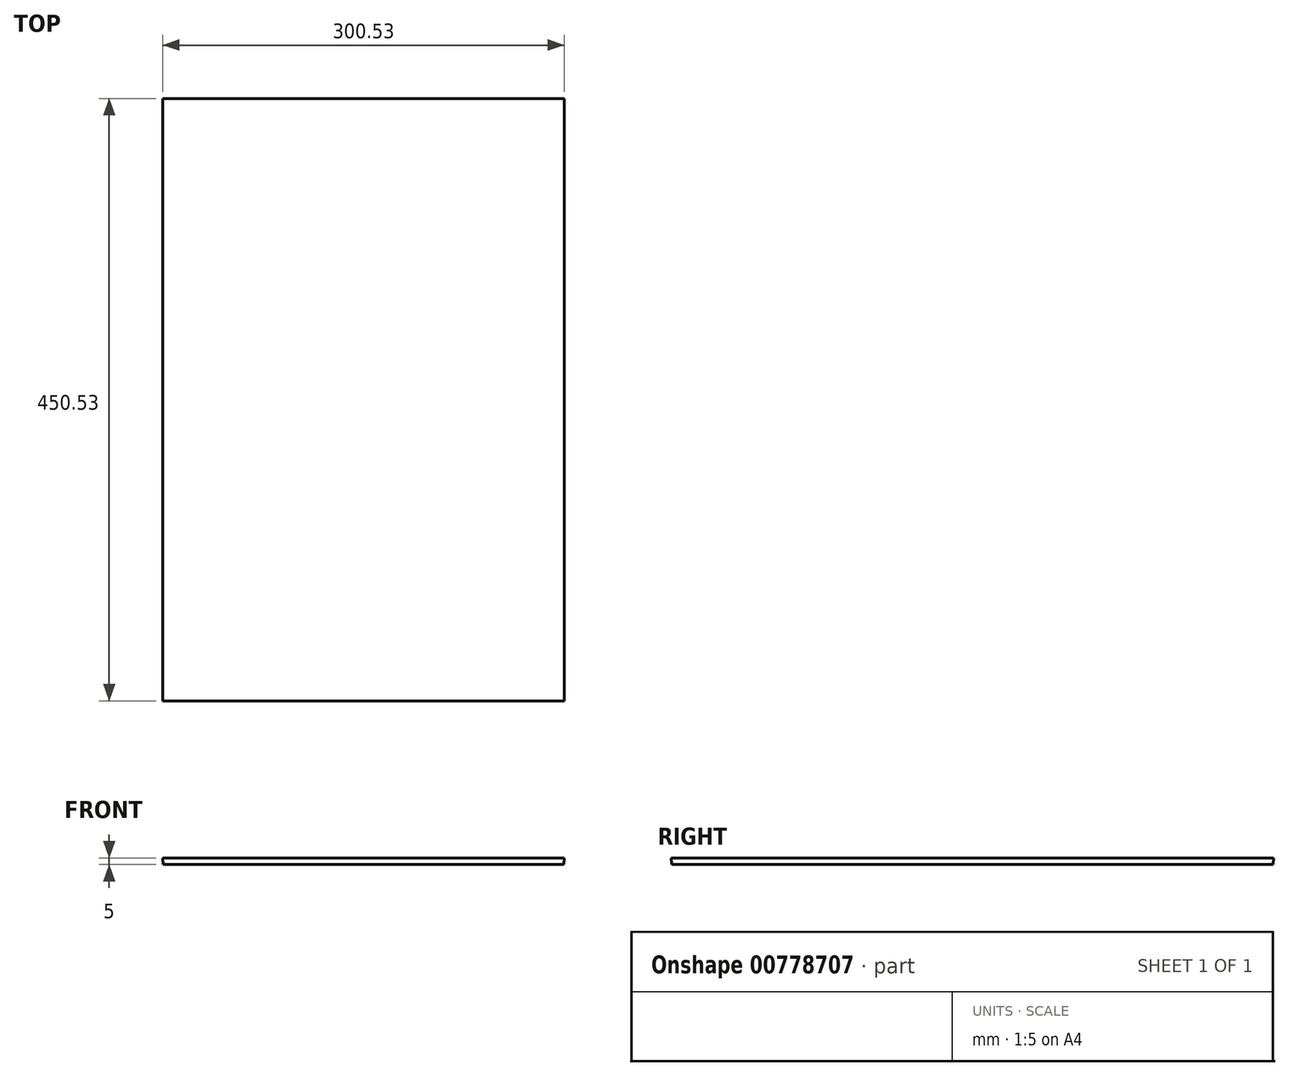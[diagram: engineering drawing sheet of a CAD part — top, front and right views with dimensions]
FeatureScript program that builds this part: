
annotation { "Feature Type Name" : "Feature", "Feature Type Description" : "" }
export const myFeature = defineFeature(function(context is Context, id is Id, definition is map)
    precondition{}
    {
        {
            var Q0;
            Q0=qCreatedBy(makeId("Top.planeOp"),FACE);
            var sketch = newSketch(context, id + "F0", { "sketchPlane" : qUnion([Q0])});
            skLineSegment(sketch, "E0.bottom", {"start": v(-180.86, 302.86) * mm, "end": v(119.14, 302.86) * mm});
            skLineSegment(sketch, "E0.top", {"start": v(-180.86, -147.14) * mm, "end": v(119.14, -147.14) * mm});
            skLineSegment(sketch, "E0.left", {"start": v(-180.86, 302.86) * mm, "end": v(-180.86, -147.14) * mm});
            skLineSegment(sketch, "E0.right", {"start": v(119.14, 302.86) * mm, "end": v(119.14, -147.14) * mm});
            skSolve(sketch);
        }
        {
            var Q0;
            Q0=makeQuery(id+"F0.imprint","IMPRINT",FACE,{"disambiguationData":[TD([[makeQuery(id+"F0.imprint","IMPRINT",EDGE,{"derivedFrom":sQuery(id+"F0.wireOp",EDGE,"E0.bottom")}),-1.0]])]});
            extrude(context, id + "F1", {"entities" : qUnion([Q0]), "depth" : 5 * mm, "offsetDistance" : 25 * mm, "hasDraft" : true, "draftAngle" : 3 * degree});
        }
    });
